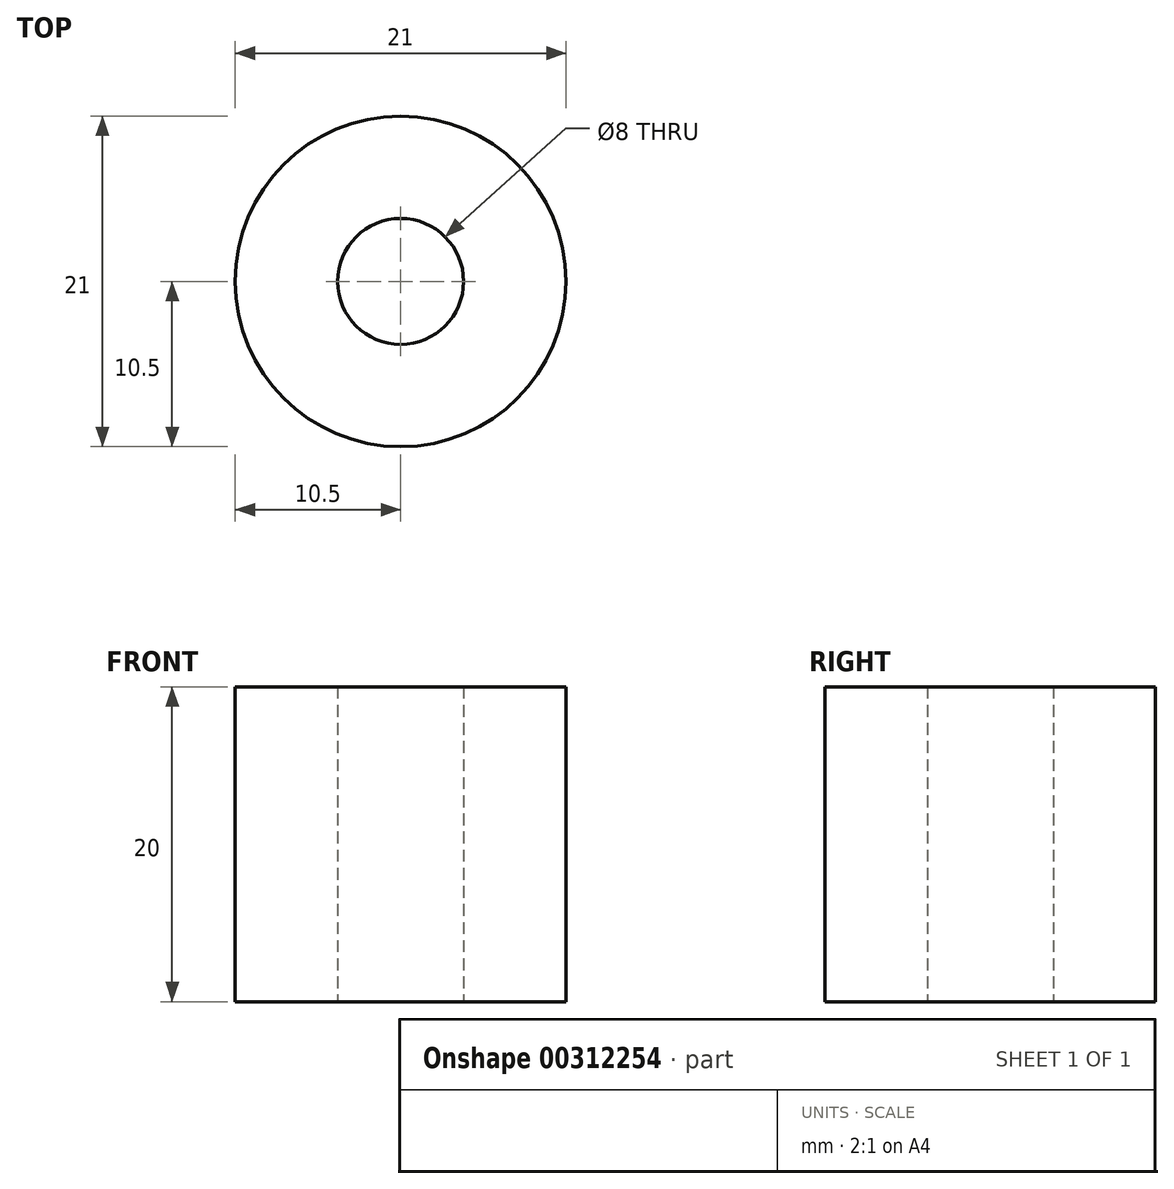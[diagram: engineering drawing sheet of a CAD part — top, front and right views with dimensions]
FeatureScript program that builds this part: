
annotation { "Feature Type Name" : "Feature", "Feature Type Description" : "" }
export const myFeature = defineFeature(function(context is Context, id is Id, definition is map)
    precondition{}
    {
        {
            var Q0;
            Q0=qCreatedBy(makeId("Top.planeOp"),FACE);
            var sketch = newSketch(context, id + "F0", { "sketchPlane" : qUnion([Q0])});
            skCircle(sketch, "E0", {"center": v(0, 0) * mm, "radius": 10.5 * mm});
            skCircle(sketch, "E1", {"center": v(0, 0) * mm, "radius": 4 * mm});
            skSolve(sketch);
        }
        {
            var Q0;
            Q0=makeQuery(id+"F0.imprint","IMPRINT",FACE,{"disambiguationData":[TD([[makeQuery(id+"F0.imprint","IMPRINT",EDGE,{"derivedFrom":sQuery(id+"F0.wireOp",EDGE,"E0")}),1.0]])]});
            extrude(context, id + "F1", {"entities" : qUnion([Q0]), "depth" : 20 * mm});
        }
    });
